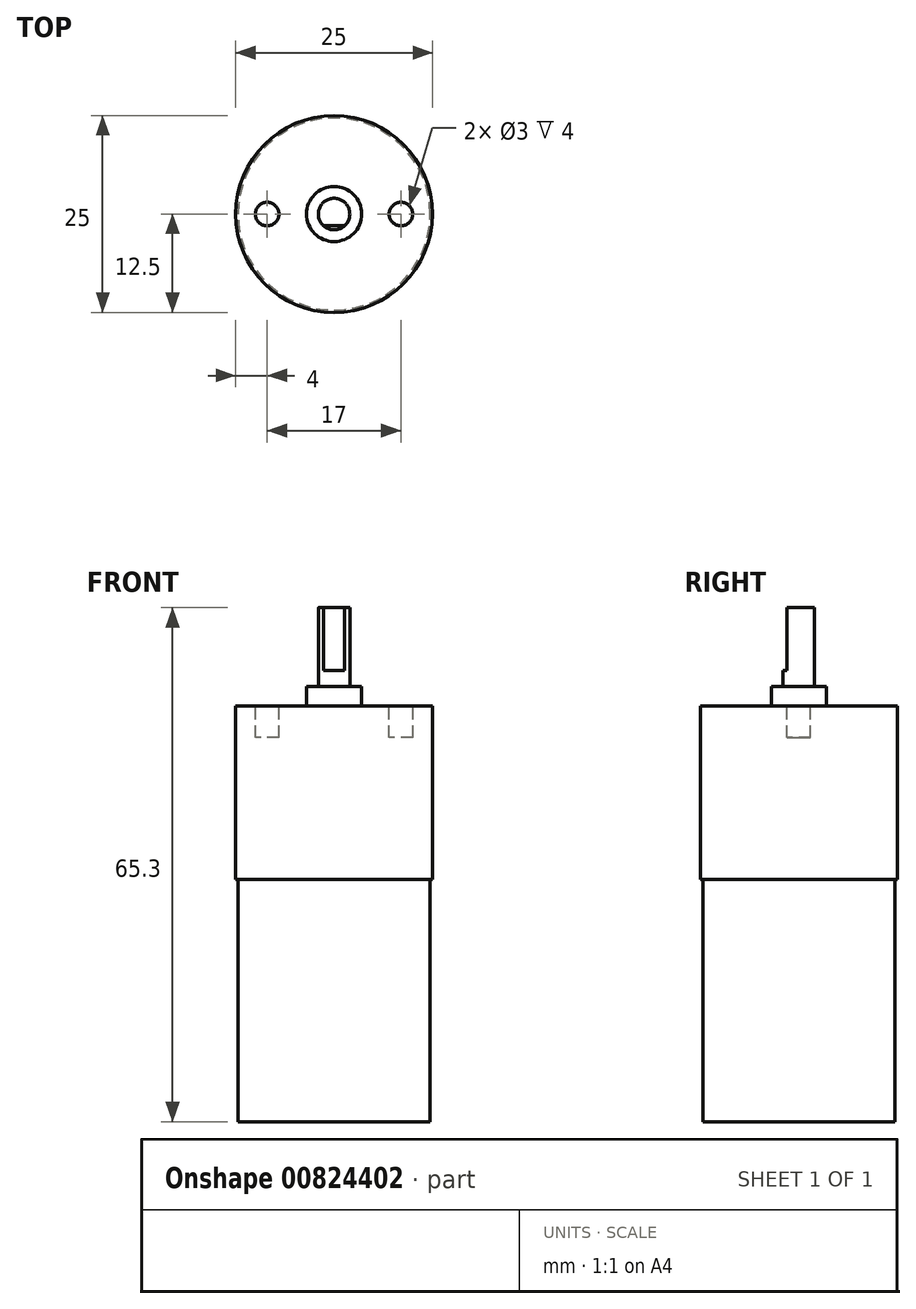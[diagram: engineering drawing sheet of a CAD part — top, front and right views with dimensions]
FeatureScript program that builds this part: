
annotation { "Feature Type Name" : "Feature", "Feature Type Description" : "" }
export const myFeature = defineFeature(function(context is Context, id is Id, definition is map)
    precondition{}
    {
        {
            var Q0;
            Q0=qCreatedBy(makeId("Top.planeOp"),FACE);
            var sketch = newSketch(context, id + "F0", { "sketchPlane" : qUnion([Q0])});
            skCircle(sketch, "E0", {"center": v(0, 0) * mm, "radius": 12.5 * mm});
            skSolve(sketch);
        }
        {
            var Q0;
            Q0=makeQuery(id+"F0.imprint","IMPRINT",FACE,{"disambiguationData":[TD([[makeQuery(id+"F0.imprint","IMPRINT",EDGE,{"derivedFrom":sQuery(id+"F0.wireOp",EDGE,"E0")}),1.0]])]});
            extrude(context, id + "F1", {"entities" : qUnion([Q0]), "oppositeDirection" : true, "depth" : 22 * mm, "offsetDistance" : 25 * mm});
        }
        {
            var Q0;
            Q0=makeQuery(id+"F1.opExtrude","CAP_FACE",FACE,{"disambiguationData":[OSD([sQuery(id+"F0.wireOp",EDGE,"E0")])],"isStart":false});
            var sketch = newSketch(context, id + "F2", { "sketchPlane" : qUnion([Q0])});
            skCircle(sketch, "E1", {"center": v(0, 0) * mm, "radius": 12.2 * mm});
            skSolve(sketch);
        }
        {
            var Q0;
            Q0=makeQuery(id+"F2.imprint","IMPRINT",FACE,{"disambiguationData":[TD([[makeQuery(id+"F2.imprint","IMPRINT",EDGE,{"derivedFrom":sQuery(id+"F2.wireOp",EDGE,"E1")}),1.0]])]});
            extrude(context, id + "F3", {"entities" : qUnion([Q0]), "operationType" : NewBodyOperationType.ADD, "depth" : 30.8 * mm, "offsetDistance" : 25 * mm});
        }
        {
            var Q0;
            Q0=makeQuery(id+"F1.opExtrude","CAP_FACE",FACE,{"disambiguationData":[OSD([sQuery(id+"F0.wireOp",EDGE,"E0")])],"isStart":true});
            var sketch = newSketch(context, id + "F4", { "sketchPlane" : qUnion([Q0])});
            skCircle(sketch, "E2", {"center": v(0, 0) * mm, "radius": 3.5 * mm});
            skSolve(sketch);
        }
        {
            var Q0;
            Q0=makeQuery(id+"F4.imprint","IMPRINT",FACE,{"disambiguationData":[TD([[makeQuery(id+"F4.imprint","IMPRINT",EDGE,{"derivedFrom":sQuery(id+"F4.wireOp",EDGE,"E2")}),1.0]])]});
            extrude(context, id + "F5", {"entities" : qUnion([Q0]), "operationType" : NewBodyOperationType.ADD, "depth" : 2.5 * mm, "offsetDistance" : 25 * mm});
        }
        {
            var Q0;
            Q0=makeQuery(id+"F1.opExtrude","CAP_FACE",FACE,{"disambiguationData":[OSD([sQuery(id+"F0.wireOp",EDGE,"E0")])],"isStart":true});
            var sketch = newSketch(context, id + "F6", { "sketchPlane" : qUnion([Q0])});
            skCircle(sketch, "E3", {"center": v(0, 0) * mm, "radius": 2 * mm});
            skSolve(sketch);
        }
        {
            var Q0;
            Q0=qSketchRegion(id+"F6",true);
            extrude(context, id + "F7", {"entities" : qUnion([Q0]), "operationType" : NewBodyOperationType.ADD, "depth" : 12.5 * mm, "offsetDistance" : 25 * mm});
        }
        {
            var Q0;
            Q0=makeQuery(id+"F7.opExtrude","CAP_FACE",FACE,{"disambiguationData":[OSD([sQuery(id+"F6.wireOp",EDGE,"E3")])],"isStart":false});
            var sketch = newSketch(context, id + "F8", { "sketchPlane" : qUnion([Q0])});
            skCircle(sketch, "E4.0.0", {"center": v(0, 0) * mm, "radius": 2 * mm});
            skLineSegment(sketch, "E5", {"start": v(-1.32, -1.5) * mm, "end": v(1.32, -1.5) * mm});
            skSolve(sketch);
        }
        {
            var Q0;
            {var subQ0=sQuery(id+"F8.wireOp",EDGE,"E5");Q0=makeQuery(id+"F8.imprint","IMPRINT",FACE,{"disambiguationData":[TD([[makeQuery(id+"F8.imprint","IMPRINT",EDGE,{"derivedFrom":subQ0}),-1.0]])]});}
            extrude(context, id + "F9", {"entities" : qUnion([Q0]), "operationType" : NewBodyOperationType.REMOVE, "oppositeDirection" : true, "depth" : 8 * mm, "offsetDistance" : 25 * mm});
        }
        {
            var Q0;
            Q0=makeQuery(id+"F1.opExtrude","CAP_FACE",FACE,{"disambiguationData":[OSD([sQuery(id+"F0.wireOp",EDGE,"E0")])],"isStart":true});
            var sketch = newSketch(context, id + "F10", { "sketchPlane" : qUnion([Q0])});
            skCircle(sketch, "E6", {"center": v(-8.5, 0) * mm, "radius": 1.5 * mm});
            skCircle(sketch, "E7", {"center": v(8.5, 0) * mm, "radius": 1.5 * mm});
            skLineSegment(sketch, "E8", {"start": v(-8.5, 0) * mm, "end": v(0, 0) * mm, "construction": true});
            skLineSegment(sketch, "E9", {"start": v(0, 0) * mm, "end": v(8.5, 0) * mm, "construction": true});
            skSolve(sketch);
        }
        {
            var Q0;
            Q0=makeQuery(id+"F10.imprint","IMPRINT",FACE,{"disambiguationData":[TD([[makeQuery(id+"F10.imprint","IMPRINT",EDGE,{"derivedFrom":sQuery(id+"F10.wireOp",EDGE,"E6")}),1.0]])]});
            var Q1;
            Q1=makeQuery(id+"F10.imprint","IMPRINT",FACE,{"disambiguationData":[TD([[makeQuery(id+"F10.imprint","IMPRINT",EDGE,{"derivedFrom":sQuery(id+"F10.wireOp",EDGE,"E7")}),1.0]])]});
            extrude(context, id + "F11", {"entities" : qUnion([Q0, Q1]), "operationType" : NewBodyOperationType.REMOVE, "oppositeDirection" : true, "depth" : 4 * mm, "offsetDistance" : 25 * mm});
        }
    });
